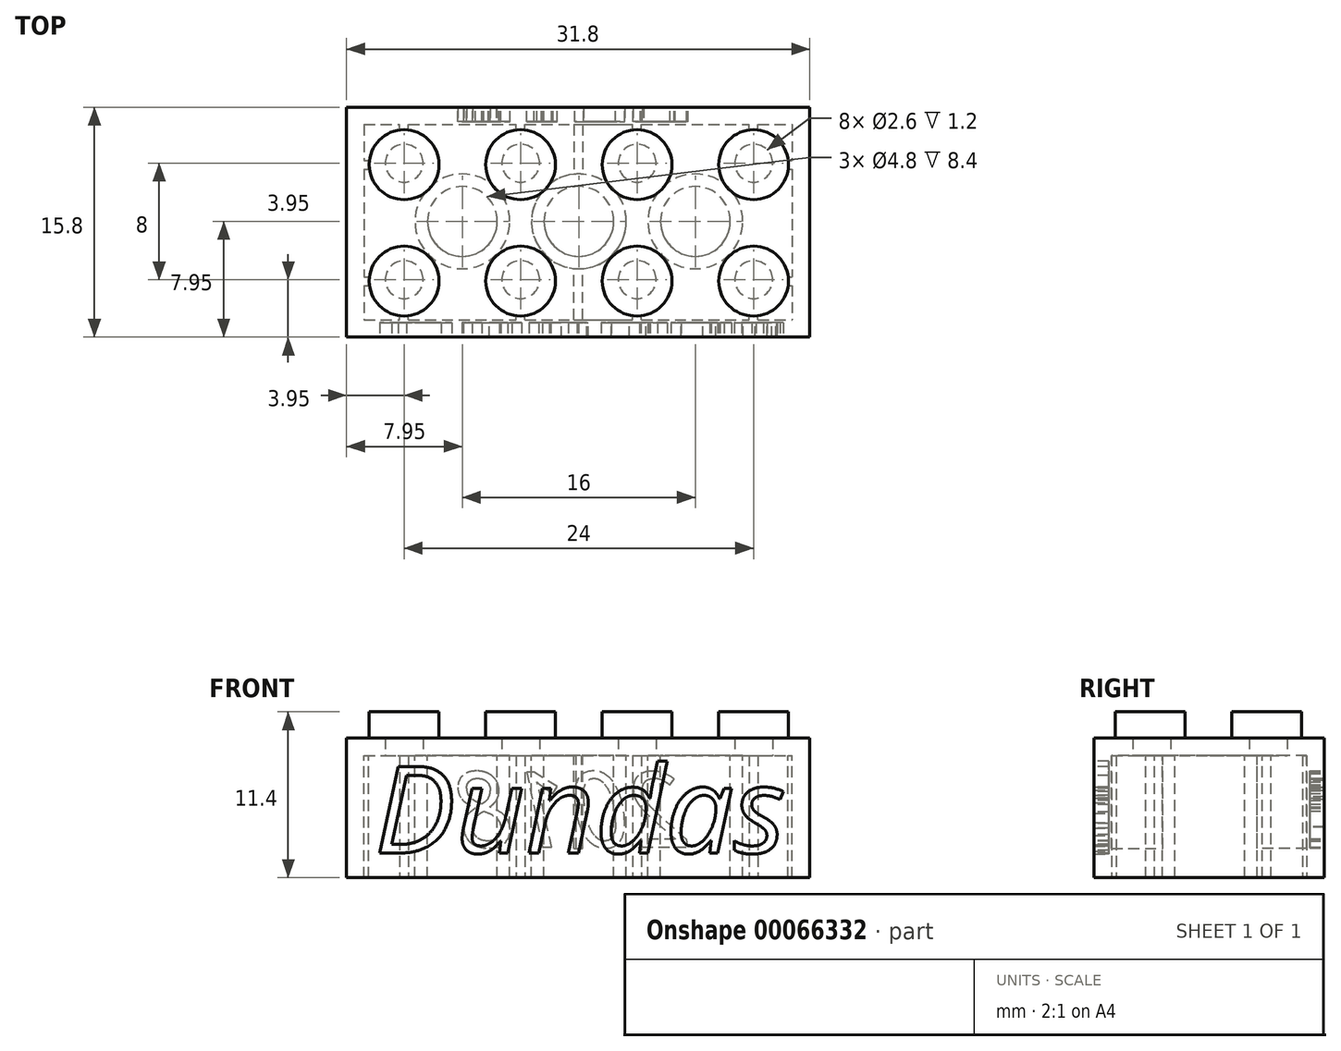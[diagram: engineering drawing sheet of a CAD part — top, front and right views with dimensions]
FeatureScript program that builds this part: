
annotation { "Feature Type Name" : "Feature", "Feature Type Description" : "" }
export const myFeature = defineFeature(function(context is Context, id is Id, definition is map)
    precondition{}
    {
        {
            var Q0;
            Q0=qCreatedBy(makeId("Top.planeOp"),FACE);
            var sketch = newSketch(context, id + "F0", { "sketchPlane" : qUnion([Q0])});
            skLineSegment(sketch, "E0.rect.bottom", {"start": v(-15.9, -7.9) * mm, "end": v(15.9, -7.9) * mm});
            skLineSegment(sketch, "E0.rect.top", {"start": v(-15.9, 7.9) * mm, "end": v(15.9, 7.9) * mm});
            skLineSegment(sketch, "E0.rect.left", {"start": v(-15.9, -7.9) * mm, "end": v(-15.9, 7.9) * mm});
            skLineSegment(sketch, "E0.rect.right", {"start": v(15.9, -7.9) * mm, "end": v(15.9, 7.9) * mm});
            skPoint(sketch, "E0.rect.middle", {"position": v(0, 0) * mm});
            skSolve(sketch);
        }
        {
            var Q0;
            Q0=makeQuery(id+"F0.imprint","IMPRINT",FACE,{"disambiguationData":[TD([[makeQuery(id+"F0.imprint","IMPRINT",EDGE,{"derivedFrom":sQuery(id+"F0.wireOp",EDGE,"E0.rect.bottom")}),1.0]])]});
            extrude(context, id + "F1", {"entities" : qUnion([Q0]), "depth" : 9.6 * mm});
        }
        {
            var Q0;
            Q0=qCreatedBy(makeId("Top.planeOp"),FACE);
            var sketch = newSketch(context, id + "F2", { "sketchPlane" : qUnion([Q0])});
            skLineSegment(sketch, "E1.rect.bottom", {"start": v(-14.7, 6.7) * mm, "end": v(14.7, 6.7) * mm});
            skLineSegment(sketch, "E1.rect.top", {"start": v(-14.7, -6.7) * mm, "end": v(14.7, -6.7) * mm});
            skLineSegment(sketch, "E1.rect.left", {"start": v(-14.7, 6.7) * mm, "end": v(-14.7, -6.7) * mm});
            skLineSegment(sketch, "E1.rect.right", {"start": v(14.7, 6.7) * mm, "end": v(14.7, -6.7) * mm});
            skPoint(sketch, "E1.rect.middle", {"position": v(0, 0) * mm});
            skSolve(sketch);
        }
        {
            var Q0;
            Q0=makeQuery(id+"F2.imprint","IMPRINT",FACE,{"disambiguationData":[TD([[makeQuery(id+"F2.imprint","IMPRINT",EDGE,{"derivedFrom":sQuery(id+"F2.wireOp",EDGE,"E1.rect.bottom")}),-1.0]])]});
            extrude(context, id + "F3", {"entities" : qUnion([Q0]), "operationType" : NewBodyOperationType.REMOVE, "depth" : 8.4 * mm});
        }
        {
            var Q0;
            Q0=makeQuery(id+"F1.opExtrude","CAP_FACE",FACE,{"disambiguationData":[OSD([sQuery(id+"F0.wireOp",EDGE,"E0.rect.bottom"),sQuery(id+"F0.wireOp",EDGE,"E0.rect.top"),sQuery(id+"F0.wireOp",EDGE,"E0.rect.left"),sQuery(id+"F0.wireOp",EDGE,"E0.rect.right")])],"isStart":false});
            var sketch = newSketch(context, id + "F4", { "sketchPlane" : qUnion([Q0])});
            skCircle(sketch, "E2", {"center": v(-11.95, 3.95) * mm, "radius": 2.4 * mm});
            skCircle(sketch, "E3.0.1.0", {"center": v(-11.95, -4.05) * mm, "radius": 2.4 * mm});
            skCircle(sketch, "E3.1.0.0", {"center": v(-3.95, 3.95) * mm, "radius": 2.4 * mm});
            skCircle(sketch, "E3.1.1.0", {"center": v(-3.95, -4.05) * mm, "radius": 2.4 * mm});
            skCircle(sketch, "E3.2.0.0", {"center": v(4.05, 3.95) * mm, "radius": 2.4 * mm});
            skCircle(sketch, "E3.2.1.0", {"center": v(4.05, -4.05) * mm, "radius": 2.4 * mm});
            skCircle(sketch, "E3.3.0.0", {"center": v(12.05, 3.95) * mm, "radius": 2.4 * mm});
            skCircle(sketch, "E3.3.1.0", {"center": v(12.05, -4.05) * mm, "radius": 2.4 * mm});
            skLineSegment(sketch, "E3.direction1", {"start": v(-11.95, 3.95) * mm, "end": v(-3.95, 3.95) * mm, "construction": true});
            skLineSegment(sketch, "E3.direction2", {"start": v(-11.95, 3.95) * mm, "end": v(-11.95, -4.05) * mm, "construction": true});
            skLineSegment(sketch, "E4", {"start": v(-11.95, -4.05) * mm, "end": v(22.18, -4.05) * mm, "construction": true});
            skLineSegment(sketch, "E5", {"start": v(22.18, -4.05) * mm, "end": v(-26.36, -4.05) * mm, "construction": true});
            skLineSegment(sketch, "E6", {"start": v(-26.36, -4.05) * mm, "end": v(-11.95, -4.05) * mm, "construction": true});
            skLineSegment(sketch, "E7", {"start": v(-11.95, -4.05) * mm, "end": v(-11.95, 22.98) * mm, "construction": true});
            skLineSegment(sketch, "E8", {"start": v(-11.95, 22.98) * mm, "end": v(-11.95, -13.82) * mm, "construction": true});
            skLineSegment(sketch, "E9", {"start": v(-11.95, -13.82) * mm, "end": v(-11.95, 3.95) * mm, "construction": true});
            skLineSegment(sketch, "E10", {"start": v(-11.95, 3.95) * mm, "end": v(-30.34, 3.95) * mm, "construction": true});
            skLineSegment(sketch, "E11", {"start": v(-30.34, 3.95) * mm, "end": v(17.8, 3.95) * mm, "construction": true});
            skLineSegment(sketch, "E12", {"start": v(17.8, 3.95) * mm, "end": v(12.05, 3.95) * mm, "construction": true});
            skLineSegment(sketch, "E13", {"start": v(12.05, 3.95) * mm, "end": v(12.05, -16.01) * mm, "construction": true});
            skLineSegment(sketch, "E14", {"start": v(12.05, -16.01) * mm, "end": v(12.05, 13.66) * mm, "construction": true});
            skLineSegment(sketch, "E15", {"start": v(12.05, 13.66) * mm, "end": v(12.05, 3.95) * mm, "construction": true});
            skLineSegment(sketch, "E16", {"start": v(4.05, 3.95) * mm, "end": v(4.05, 14.31) * mm, "construction": true});
            skLineSegment(sketch, "E17", {"start": v(4.05, 14.31) * mm, "end": v(4.05, -13.22) * mm, "construction": true});
            skLineSegment(sketch, "E18", {"start": v(4.05, -13.22) * mm, "end": v(4.05, -4.05) * mm, "construction": true});
            skLineSegment(sketch, "E19", {"start": v(-3.95, -4.05) * mm, "end": v(-3.95, -14.7) * mm, "construction": true});
            skLineSegment(sketch, "E20", {"start": v(-3.95, -14.7) * mm, "end": v(-3.95, 14.43) * mm, "construction": true});
            skLineSegment(sketch, "E21", {"start": v(-3.95, 14.43) * mm, "end": v(-3.95, 3.95) * mm, "construction": true});
            skSolve(sketch);
        }
        {
            var Q0;
            Q0 = qSketchRegion(id + "F4", true);
            extrude(context, id + "F5", {"entities" : qUnion([Q0]), "operationType" : NewBodyOperationType.ADD, "depth" : 1.8 * mm});
        }
        {
            var Q0;
            Q0=makeQuery(id+"F3.boolean.opBoolean","COPY",FACE,{"derivedFrom":makeQuery(id+"F3.opExtrude","CAP_FACE",FACE,{"disambiguationData":[OSD([sQuery(id+"F2.wireOp",EDGE,"E1.rect.bottom"),sQuery(id+"F2.wireOp",EDGE,"E1.rect.top"),sQuery(id+"F2.wireOp",EDGE,"E1.rect.left"),sQuery(id+"F2.wireOp",EDGE,"E1.rect.right")])],"isStart":false})});
            var sketch = newSketch(context, id + "F6", { "sketchPlane" : qUnion([Q0])});
            skCircle(sketch, "E22", {"center": v(-11.95, 3.95) * mm, "radius": 1.3 * mm});
            skCircle(sketch, "E23.0.1.0", {"center": v(-11.95, -4.05) * mm, "radius": 1.3 * mm});
            skCircle(sketch, "E23.1.0.0", {"center": v(-3.95, 3.95) * mm, "radius": 1.3 * mm});
            skCircle(sketch, "E23.1.1.0", {"center": v(-3.95, -4.05) * mm, "radius": 1.3 * mm});
            skCircle(sketch, "E23.2.0.0", {"center": v(4.05, 3.95) * mm, "radius": 1.3 * mm});
            skCircle(sketch, "E23.2.1.0", {"center": v(4.05, -4.05) * mm, "radius": 1.3 * mm});
            skCircle(sketch, "E23.3.0.0", {"center": v(12.05, 3.95) * mm, "radius": 1.3 * mm});
            skCircle(sketch, "E23.3.1.0", {"center": v(12.05, -4.05) * mm, "radius": 1.3 * mm});
            skLineSegment(sketch, "E23.direction1", {"start": v(-11.95, 3.95) * mm, "end": v(-3.95, 3.95) * mm, "construction": true});
            skLineSegment(sketch, "E23.direction2", {"start": v(-11.95, 3.95) * mm, "end": v(-11.95, -4.05) * mm, "construction": true});
            skLineSegment(sketch, "E24", {"start": v(-3.95, 3.95) * mm, "end": v(-11.95, -4.05) * mm, "construction": true});
            skSolve(sketch);
        }
        {
            var Q0;
            Q0 = qSketchRegion(id + "F6", true);
            extrude(context, id + "F7", {"entities" : qUnion([Q0]), "operationType" : NewBodyOperationType.REMOVE, "oppositeDirection" : true, "depth" : 1.2 * mm});
        }
        {
            var Q0;
            Q0=makeQuery(id+"F1.opExtrude","SWEPT_FACE",FACE,{"disambiguationData":[OSD([sQuery(id+"F0.wireOp",EDGE,"E0.rect.bottom")])]});
            var sketch = newSketch(context, id + "F8", { "sketchPlane" : qUnion([Q0])});
            skText(sketch, "E25", { "text": "Dundas", "fontName": "OpenSans-Italic.ttf"});
            const initialGuessF8  = {"E25": [-0.01397, 0.0017, 1, 0, 0.00599]};
            skSetInitialGuess(sketch, initialGuessF8);
            skSolve(sketch);
        }
        {
            var Q0;
            Q0 = qSketchRegion(id + "F8", true);
            extrude(context, id + "F9", {"entities" : qUnion([Q0]), "operationType" : NewBodyOperationType.REMOVE, "oppositeDirection" : true, "depth" : 1 * mm});
        }
        {
            var Q0;
            Q0=makeQuery(id+"F1.opExtrude","SWEPT_FACE",FACE,{"disambiguationData":[OSD([sQuery(id+"F0.wireOp",EDGE,"E0.rect.top")])]});
            var sketch = newSketch(context, id + "F10", { "sketchPlane" : qUnion([Q0])});
            skText(sketch, "E26", { "text": "2018", "fontName": "OpenSans-Italic.ttf"});
            const initialGuessF10  = {"E26": [-0.00759, 0.0021, 1, 0, 0.0052]};
            skSetInitialGuess(sketch, initialGuessF10);
            skSolve(sketch);
        }
        {
            var Q0;
            Q0 = qSketchRegion(id + "F10", true);
            extrude(context, id + "F11", {"entities" : qUnion([Q0]), "operationType" : NewBodyOperationType.REMOVE, "oppositeDirection" : true, "depth" : 1 * mm});
        }
        {
            var Q0;
            Q0=makeQuery(id+"F1.opExtrude","CAP_FACE",FACE,{"disambiguationData":[OSD([sQuery(id+"F0.wireOp",EDGE,"E0.rect.bottom"),sQuery(id+"F0.wireOp",EDGE,"E0.rect.top"),sQuery(id+"F0.wireOp",EDGE,"E0.rect.left"),sQuery(id+"F0.wireOp",EDGE,"E0.rect.right")])],"isStart":true});
            var sketch = newSketch(context, id + "F12", { "sketchPlane" : qUnion([Q0])});
            skLineSegment(sketch, "E27", {"start": v(-11.95, -3.95) * mm, "end": v(-11.95, 10.28) * mm, "construction": true});
            skLineSegment(sketch, "E28.bottom", {"start": v(-12.25, 6.7) * mm, "end": v(-11.65, 6.7) * mm});
            skLineSegment(sketch, "E28.top", {"start": v(-12.25, 6.4) * mm, "end": v(-11.65, 6.4) * mm});
            skLineSegment(sketch, "E28.left", {"start": v(-12.25, 6.7) * mm, "end": v(-12.25, 6.4) * mm});
            skLineSegment(sketch, "E28.right", {"start": v(-11.65, 6.7) * mm, "end": v(-11.65, 6.4) * mm});
            skLineSegment(sketch, "E29.0.1.0", {"start": v(-11.65, -6.4) * mm, "end": v(-11.65, -6.7) * mm});
            skLineSegment(sketch, "E29.0.1.1", {"start": v(-12.25, -6.4) * mm, "end": v(-11.65, -6.4) * mm});
            skLineSegment(sketch, "E29.0.1.2", {"start": v(-12.25, -6.4) * mm, "end": v(-12.25, -6.7) * mm});
            skLineSegment(sketch, "E29.0.1.3", {"start": v(-12.25, -6.7) * mm, "end": v(-11.65, -6.7) * mm});
            skLineSegment(sketch, "E29.1.0.0", {"start": v(-3.65, 6.7) * mm, "end": v(-3.65, 6.4) * mm});
            skLineSegment(sketch, "E29.1.0.1", {"start": v(-4.25, 6.7) * mm, "end": v(-3.65, 6.7) * mm});
            skLineSegment(sketch, "E29.1.0.2", {"start": v(-4.25, 6.7) * mm, "end": v(-4.25, 6.4) * mm});
            skLineSegment(sketch, "E29.1.0.3", {"start": v(-4.25, 6.4) * mm, "end": v(-3.65, 6.4) * mm});
            skLineSegment(sketch, "E29.1.1.0", {"start": v(-3.65, -6.4) * mm, "end": v(-3.65, -6.7) * mm});
            skLineSegment(sketch, "E29.1.1.1", {"start": v(-4.25, -6.4) * mm, "end": v(-3.65, -6.4) * mm});
            skLineSegment(sketch, "E29.1.1.2", {"start": v(-4.25, -6.4) * mm, "end": v(-4.25, -6.7) * mm});
            skLineSegment(sketch, "E29.1.1.3", {"start": v(-4.25, -6.7) * mm, "end": v(-3.65, -6.7) * mm});
            skLineSegment(sketch, "E29.2.0.0", {"start": v(4.35, 6.7) * mm, "end": v(4.35, 6.4) * mm});
            skLineSegment(sketch, "E29.2.0.1", {"start": v(3.75, 6.7) * mm, "end": v(4.35, 6.7) * mm});
            skLineSegment(sketch, "E29.2.0.2", {"start": v(3.75, 6.7) * mm, "end": v(3.75, 6.4) * mm});
            skLineSegment(sketch, "E29.2.0.3", {"start": v(3.75, 6.4) * mm, "end": v(4.35, 6.4) * mm});
            skLineSegment(sketch, "E29.2.1.0", {"start": v(4.35, -6.4) * mm, "end": v(4.35, -6.7) * mm});
            skLineSegment(sketch, "E29.2.1.1", {"start": v(3.75, -6.4) * mm, "end": v(4.35, -6.4) * mm});
            skLineSegment(sketch, "E29.2.1.2", {"start": v(3.75, -6.4) * mm, "end": v(3.75, -6.7) * mm});
            skLineSegment(sketch, "E29.2.1.3", {"start": v(3.75, -6.7) * mm, "end": v(4.35, -6.7) * mm});
            skLineSegment(sketch, "E29.3.0.0", {"start": v(12.35, 6.7) * mm, "end": v(12.35, 6.4) * mm});
            skLineSegment(sketch, "E29.3.0.1", {"start": v(11.75, 6.7) * mm, "end": v(12.35, 6.7) * mm});
            skLineSegment(sketch, "E29.3.0.2", {"start": v(11.75, 6.7) * mm, "end": v(11.75, 6.4) * mm});
            skLineSegment(sketch, "E29.3.0.3", {"start": v(11.75, 6.4) * mm, "end": v(12.35, 6.4) * mm});
            skLineSegment(sketch, "E29.3.1.0", {"start": v(12.35, -6.4) * mm, "end": v(12.35, -6.7) * mm});
            skLineSegment(sketch, "E29.3.1.1", {"start": v(11.75, -6.4) * mm, "end": v(12.35, -6.4) * mm});
            skLineSegment(sketch, "E29.3.1.2", {"start": v(11.75, -6.4) * mm, "end": v(11.75, -6.7) * mm});
            skLineSegment(sketch, "E29.3.1.3", {"start": v(11.75, -6.7) * mm, "end": v(12.35, -6.7) * mm});
            skLineSegment(sketch, "E29.direction1", {"start": v(-11.65, 6.4) * mm, "end": v(-3.65, 6.4) * mm, "construction": true});
            skLineSegment(sketch, "E29.direction2", {"start": v(-11.65, 6.4) * mm, "end": v(-11.65, -6.7) * mm, "construction": true});
            skSolve(sketch);
        }
        {
            var Q0;
            Q0 = qSketchRegion(id + "F12", true);
            var Q1;
            Q1=makeQuery(id+"F3.boolean.opBoolean","COPY",FACE,{"derivedFrom":makeQuery(id+"F3.opExtrude","CAP_FACE",FACE,{"disambiguationData":[OSD([sQuery(id+"F2.wireOp",EDGE,"E1.rect.bottom"),sQuery(id+"F2.wireOp",EDGE,"E1.rect.top"),sQuery(id+"F2.wireOp",EDGE,"E1.rect.left"),sQuery(id+"F2.wireOp",EDGE,"E1.rect.right")])],"isStart":false})});
            extrude(context, id + "F13", {"entities" : qUnion([Q0]), "operationType" : NewBodyOperationType.ADD, "endBound" : BoundingType.UP_TO_SURFACE, "oppositeDirection" : true, "endBoundEntityFace" : qUnion([Q1]), "depth" : 25 * mm});
        }
        {
            var Q0;
            Q0=makeQuery(id+"F3.boolean.opBoolean","COPY",FACE,{"derivedFrom":makeQuery(id+"F3.opExtrude","CAP_FACE",FACE,{"disambiguationData":[OSD([sQuery(id+"F2.wireOp",EDGE,"E1.rect.bottom"),sQuery(id+"F2.wireOp",EDGE,"E1.rect.top"),sQuery(id+"F2.wireOp",EDGE,"E1.rect.left"),sQuery(id+"F2.wireOp",EDGE,"E1.rect.right")])],"isStart":false})});
            var sketch = newSketch(context, id + "F14", { "sketchPlane" : qUnion([Q0])});
            skLineSegment(sketch, "E30.bottom", {"start": v(-14.7, -3.65) * mm, "end": v(-14.4, -3.65) * mm});
            skLineSegment(sketch, "E30.top", {"start": v(-14.7, -4.25) * mm, "end": v(-14.4, -4.25) * mm});
            skLineSegment(sketch, "E30.left", {"start": v(-14.7, -3.65) * mm, "end": v(-14.7, -4.25) * mm});
            skLineSegment(sketch, "E30.right", {"start": v(-14.4, -3.65) * mm, "end": v(-14.4, -4.25) * mm});
            skLineSegment(sketch, "E31.0.1.0", {"start": v(-14.4, 4.35) * mm, "end": v(-14.4, 3.75) * mm});
            skLineSegment(sketch, "E31.0.1.1", {"start": v(-14.7, 4.35) * mm, "end": v(-14.4, 4.35) * mm});
            skLineSegment(sketch, "E31.0.1.2", {"start": v(-14.7, 4.35) * mm, "end": v(-14.7, 3.75) * mm});
            skLineSegment(sketch, "E31.0.1.3", {"start": v(-14.7, 3.75) * mm, "end": v(-14.4, 3.75) * mm});
            skLineSegment(sketch, "E31.1.0.0", {"start": v(14.7, -3.65) * mm, "end": v(14.7, -4.25) * mm});
            skLineSegment(sketch, "E31.1.0.1", {"start": v(14.4, -3.65) * mm, "end": v(14.7, -3.65) * mm});
            skLineSegment(sketch, "E31.1.0.2", {"start": v(14.4, -3.65) * mm, "end": v(14.4, -4.25) * mm});
            skLineSegment(sketch, "E31.1.0.3", {"start": v(14.4, -4.25) * mm, "end": v(14.7, -4.25) * mm});
            skLineSegment(sketch, "E31.1.1.0", {"start": v(14.7, 4.35) * mm, "end": v(14.7, 3.75) * mm});
            skLineSegment(sketch, "E31.1.1.1", {"start": v(14.4, 4.35) * mm, "end": v(14.7, 4.35) * mm});
            skLineSegment(sketch, "E31.1.1.2", {"start": v(14.4, 4.35) * mm, "end": v(14.4, 3.75) * mm});
            skLineSegment(sketch, "E31.1.1.3", {"start": v(14.4, 3.75) * mm, "end": v(14.7, 3.75) * mm});
            skLineSegment(sketch, "E31.direction1", {"start": v(-14.4, -4.25) * mm, "end": v(14.7, -4.25) * mm, "construction": true});
            skLineSegment(sketch, "E31.direction2", {"start": v(-14.4, -4.25) * mm, "end": v(-14.4, 3.75) * mm, "construction": true});
            skSolve(sketch);
        }
        {
            var Q0;
            Q0 = qSketchRegion(id + "F14", true);
            extrude(context, id + "F15", {"entities" : qUnion([Q0]), "operationType" : NewBodyOperationType.ADD, "depth" : 8.4 * mm});
        }
        {
            var Q0;
            Q0=makeQuery(id+"F3.boolean.opBoolean","COPY",FACE,{"derivedFrom":makeQuery(id+"F3.opExtrude","CAP_FACE",FACE,{"disambiguationData":[OSD([sQuery(id+"F2.wireOp",EDGE,"E1.rect.bottom"),sQuery(id+"F2.wireOp",EDGE,"E1.rect.top"),sQuery(id+"F2.wireOp",EDGE,"E1.rect.left"),sQuery(id+"F2.wireOp",EDGE,"E1.rect.right")])],"isStart":false})});
            var sketch = newSketch(context, id + "F16", { "sketchPlane" : qUnion([Q0])});
            skPoint(sketch, "E32.rect.middle", {"position": v(0, 0) * mm});
            skLineSegment(sketch, "E33.rect.bottom", {"start": v(-0.3, -6.7) * mm, "end": v(0.3, -6.7) * mm});
            skLineSegment(sketch, "E33.rect.top", {"start": v(-0.3, -3.23) * mm, "end": v(0.3, -3.23) * mm});
            skLineSegment(sketch, "E33.rect.left", {"start": v(-0.3, -6.7) * mm, "end": v(-0.3, -3.23) * mm});
            skLineSegment(sketch, "E33.rect.right", {"start": v(0.3, -6.7) * mm, "end": v(0.3, -3.23) * mm});
            skPoint(sketch, "E33.rect.middle", {"position": v(0, -4.97) * mm});
            skLineSegment(sketch, "E34.rect.bottom", {"start": v(-0.3, 6.7) * mm, "end": v(0.3, 6.7) * mm});
            skLineSegment(sketch, "E34.rect.top", {"start": v(-0.3, 3.2) * mm, "end": v(0.3, 3.2) * mm});
            skLineSegment(sketch, "E34.rect.left", {"start": v(-0.3, 6.7) * mm, "end": v(-0.3, 3.2) * mm});
            skLineSegment(sketch, "E34.rect.right", {"start": v(0.3, 6.7) * mm, "end": v(0.3, 3.2) * mm});
            skPoint(sketch, "E34.rect.middle", {"position": v(0, 4.95) * mm});
            skSolve(sketch);
        }
        {
            var Q0;
            Q0 = qSketchRegion(id + "F16", true);
            extrude(context, id + "F17", {"entities" : qUnion([Q0]), "operationType" : NewBodyOperationType.ADD, "depth" : 6.4 * mm});
        }
        {
            var Q0;
            Q0=makeQuery(id+"F6.imprint","IMPRINT",FACE,{"disambiguationData":[TD([[makeQuery(id+"F6.imprint","IMPRINT",EDGE,{"derivedFrom":sQuery(id+"F6.wireOp",EDGE,"E22")}),-1.0]])]});
            var sketch = newSketch(context, id + "F18", { "sketchPlane" : qUnion([Q0])});
            skCircle(sketch, "E35", {"center": v(-7.95, -0.05) * mm, "radius": 3.25 * mm});
            skCircle(sketch, "E36", {"center": v(-7.95, -0.05) * mm, "radius": 2.4 * mm});
            skCircle(sketch, "E37.1.0.0", {"center": v(0.05, -0.05) * mm, "radius": 2.4 * mm});
            skCircle(sketch, "E37.1.0.1", {"center": v(0.05, -0.05) * mm, "radius": 3.25 * mm});
            skCircle(sketch, "E37.2.0.0", {"center": v(8.05, -0.05) * mm, "radius": 2.4 * mm});
            skCircle(sketch, "E37.2.0.1", {"center": v(8.05, -0.05) * mm, "radius": 3.25 * mm});
            skLineSegment(sketch, "E37.direction1", {"start": v(-7.95, -0.05) * mm, "end": v(0.05, -0.05) * mm, "construction": true});
            skSolve(sketch);
        }
        {
            var Q0;
            Q0 = qSketchRegion(id + "F18", true);
            var Q1;
            Q1=makeQuery(id+"F15.boolean.opBoolean","MERGE",FACE,{"derivedFrom":[makeQuery(id+"F13.boolean.opBoolean","MERGE",FACE,{"derivedFrom":[makeQuery(id+"F1.opExtrude","CAP_FACE",FACE,{"disambiguationData":[OSD([sQuery(id+"F0.wireOp",EDGE,"E0.rect.bottom"),sQuery(id+"F0.wireOp",EDGE,"E0.rect.top"),sQuery(id+"F0.wireOp",EDGE,"E0.rect.left"),sQuery(id+"F0.wireOp",EDGE,"E0.rect.right")])],"isStart":true}),makeQuery(id+"F13.opExtrude","CAP_FACE",FACE,{"disambiguationData":[OSD([sQuery(id+"F12.wireOp",EDGE,"E28.bottom"),sQuery(id+"F12.wireOp",EDGE,"E28.top"),sQuery(id+"F12.wireOp",EDGE,"E28.left"),sQuery(id+"F12.wireOp",EDGE,"E28.right")])],"isStart":true}),makeQuery(id+"F13.opExtrude","CAP_FACE",FACE,{"disambiguationData":[OSD([sQuery(id+"F12.wireOp",EDGE,"E29.0.1.0"),sQuery(id+"F12.wireOp",EDGE,"E29.0.1.1"),sQuery(id+"F12.wireOp",EDGE,"E29.0.1.2"),sQuery(id+"F12.wireOp",EDGE,"E29.0.1.3")])],"isStart":true}),makeQuery(id+"F13.opExtrude","CAP_FACE",FACE,{"disambiguationData":[OSD([sQuery(id+"F12.wireOp",EDGE,"E29.1.0.0"),sQuery(id+"F12.wireOp",EDGE,"E29.1.0.1"),sQuery(id+"F12.wireOp",EDGE,"E29.1.0.2"),sQuery(id+"F12.wireOp",EDGE,"E29.1.0.3")])],"isStart":true}),makeQuery(id+"F13.opExtrude","CAP_FACE",FACE,{"disambiguationData":[OSD([sQuery(id+"F12.wireOp",EDGE,"E29.1.1.0"),sQuery(id+"F12.wireOp",EDGE,"E29.1.1.1"),sQuery(id+"F12.wireOp",EDGE,"E29.1.1.2"),sQuery(id+"F12.wireOp",EDGE,"E29.1.1.3")])],"isStart":true}),makeQuery(id+"F13.opExtrude","CAP_FACE",FACE,{"disambiguationData":[OSD([sQuery(id+"F12.wireOp",EDGE,"E29.2.0.0"),sQuery(id+"F12.wireOp",EDGE,"E29.2.0.1"),sQuery(id+"F12.wireOp",EDGE,"E29.2.0.2"),sQuery(id+"F12.wireOp",EDGE,"E29.2.0.3")])],"isStart":true}),makeQuery(id+"F13.opExtrude","CAP_FACE",FACE,{"disambiguationData":[OSD([sQuery(id+"F12.wireOp",EDGE,"E29.2.1.0"),sQuery(id+"F12.wireOp",EDGE,"E29.2.1.1"),sQuery(id+"F12.wireOp",EDGE,"E29.2.1.2"),sQuery(id+"F12.wireOp",EDGE,"E29.2.1.3")])],"isStart":true}),makeQuery(id+"F13.opExtrude","CAP_FACE",FACE,{"disambiguationData":[OSD([sQuery(id+"F12.wireOp",EDGE,"E29.3.0.0"),sQuery(id+"F12.wireOp",EDGE,"E29.3.0.1"),sQuery(id+"F12.wireOp",EDGE,"E29.3.0.2"),sQuery(id+"F12.wireOp",EDGE,"E29.3.0.3")])],"isStart":true}),makeQuery(id+"F13.opExtrude","CAP_FACE",FACE,{"disambiguationData":[OSD([sQuery(id+"F12.wireOp",EDGE,"E29.3.1.0"),sQuery(id+"F12.wireOp",EDGE,"E29.3.1.1"),sQuery(id+"F12.wireOp",EDGE,"E29.3.1.2"),sQuery(id+"F12.wireOp",EDGE,"E29.3.1.3")])],"isStart":true})]}),makeQuery(id+"F15.opExtrude","CAP_FACE",FACE,{"disambiguationData":[OSD([sQuery(id+"F14.wireOp",EDGE,"E30.bottom"),sQuery(id+"F14.wireOp",EDGE,"E30.top"),sQuery(id+"F14.wireOp",EDGE,"E30.left"),sQuery(id+"F14.wireOp",EDGE,"E30.right")])],"isStart":false}),makeQuery(id+"F15.opExtrude","CAP_FACE",FACE,{"disambiguationData":[OSD([sQuery(id+"F14.wireOp",EDGE,"E31.0.1.0"),sQuery(id+"F14.wireOp",EDGE,"E31.0.1.1"),sQuery(id+"F14.wireOp",EDGE,"E31.0.1.2"),sQuery(id+"F14.wireOp",EDGE,"E31.0.1.3")])],"isStart":false}),makeQuery(id+"F15.opExtrude","CAP_FACE",FACE,{"disambiguationData":[OSD([sQuery(id+"F14.wireOp",EDGE,"E31.1.0.0"),sQuery(id+"F14.wireOp",EDGE,"E31.1.0.1"),sQuery(id+"F14.wireOp",EDGE,"E31.1.0.2"),sQuery(id+"F14.wireOp",EDGE,"E31.1.0.3")])],"isStart":false}),makeQuery(id+"F15.opExtrude","CAP_FACE",FACE,{"disambiguationData":[OSD([sQuery(id+"F14.wireOp",EDGE,"E31.1.1.0"),sQuery(id+"F14.wireOp",EDGE,"E31.1.1.1"),sQuery(id+"F14.wireOp",EDGE,"E31.1.1.2"),sQuery(id+"F14.wireOp",EDGE,"E31.1.1.3")])],"isStart":false})]});
            extrude(context, id + "F19", {"entities" : qUnion([Q0]), "operationType" : NewBodyOperationType.ADD, "endBound" : BoundingType.UP_TO_SURFACE, "endBoundEntityFace" : qUnion([Q1]), "depth" : 25 * mm});
        }
    });
